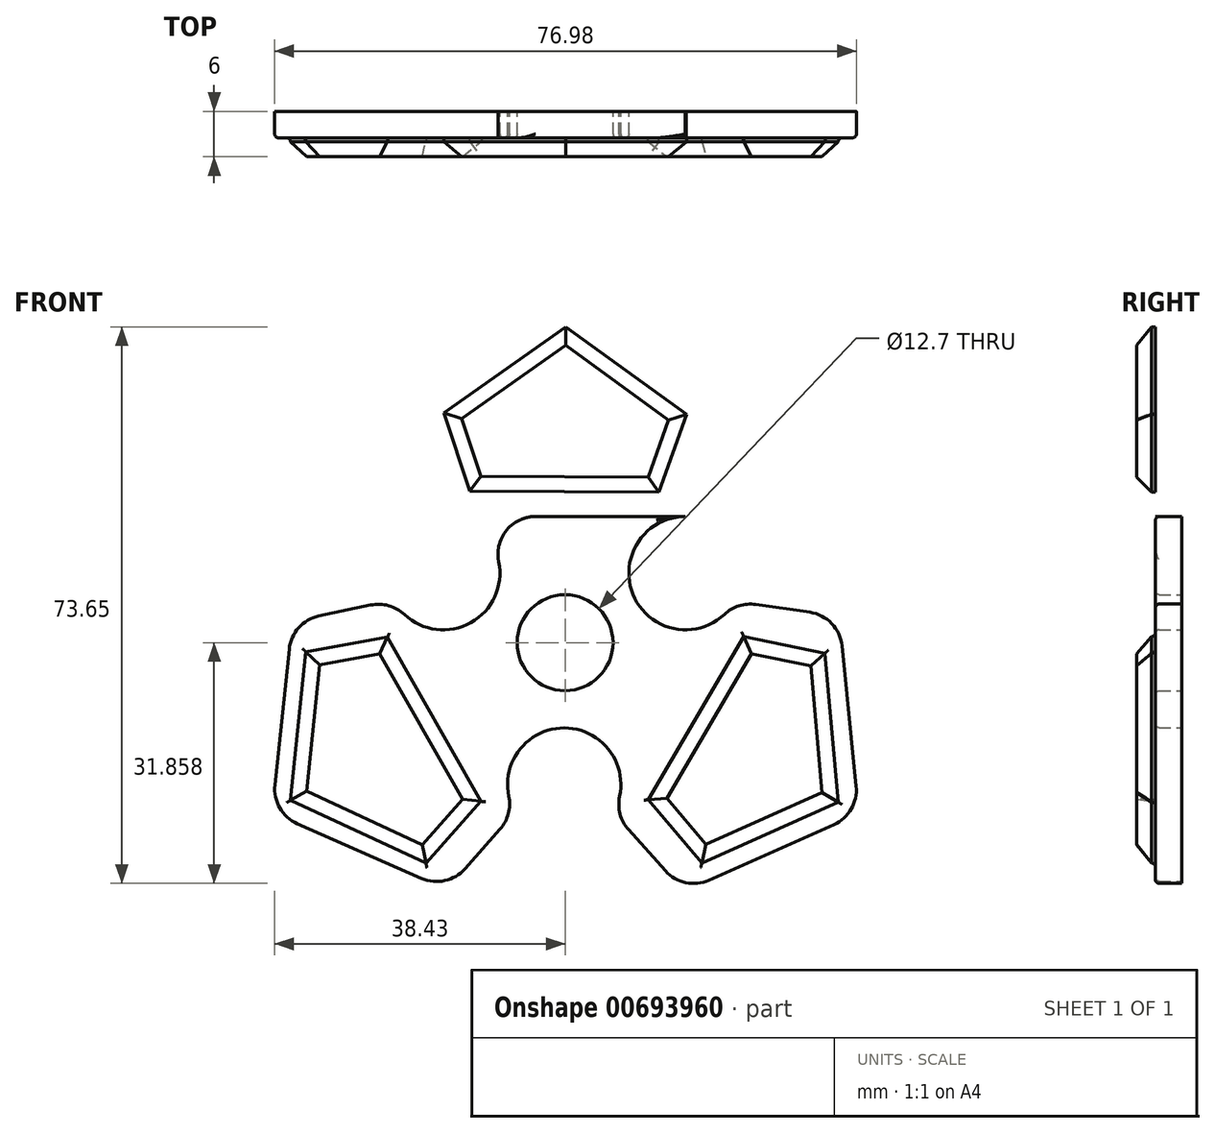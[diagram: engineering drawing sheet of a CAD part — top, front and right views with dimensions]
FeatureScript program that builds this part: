
annotation { "Feature Type Name" : "Feature", "Feature Type Description" : "" }
export const myFeature = defineFeature(function(context is Context, id is Id, definition is map)
    precondition{}
    {
        {
            var Q0;
            Q0=qCreatedBy(makeId("Front.planeOp"),FACE);
            var sketch = newSketch(context, id + "F0", { "sketchPlane" : qUnion([Q0])});
            skPoint(sketch, "E0.center", {"position": v(-0.03, -0.92) * mm});
            skLineSegment(sketch, "E1.0", {"start": v(15.99, 15.77) * mm, "end": v(-16.16, 15.77) * mm});
            skLineSegment(sketch, "E1.1", {"start": v(-16.16, 15.77) * mm, "end": v(-20.52, 29.1) * mm});
            skLineSegment(sketch, "E1.2", {"start": v(-20.52, 29.1) * mm, "end": v(0, 44.01) * mm});
            skLineSegment(sketch, "E1.3", {"start": v(0, 44.01) * mm, "end": v(20.51, 29.1) * mm});
            skLineSegment(sketch, "E1.4", {"start": v(20.51, 29.1) * mm, "end": v(15.99, 15.77) * mm});
            skPoint(sketch, "E1.0.midPoint", {"position": v(-0.09, 15.77) * mm});
            skLineSegment(sketch, "E2.1.0", {"start": v(22.42, 4.54) * mm, "end": v(36.23, 2.53) * mm});
            skLineSegment(sketch, "E2.1.2", {"start": v(36.23, 2.53) * mm, "end": v(38.86, -23.51) * mm});
            skLineSegment(sketch, "E2.1.3", {"start": v(6.36, -23.44) * mm, "end": v(22.42, 4.54) * mm});
            skLineSegment(sketch, "E2.1.4", {"start": v(15.7, -33.83) * mm, "end": v(6.36, -23.44) * mm});
            skLineSegment(sketch, "E2.1.5", {"start": v(38.86, -23.51) * mm, "end": v(15.7, -33.83) * mm});
            skLineSegment(sketch, "E2.2.0", {"start": v(-6.68, -23.39) * mm, "end": v(-15.67, -33.57) * mm});
            skLineSegment(sketch, "E2.2.2", {"start": v(-15.67, -33.57) * mm, "end": v(-38.81, -23.39) * mm});
            skLineSegment(sketch, "E2.2.3", {"start": v(-22.75, 4.69) * mm, "end": v(-6.68, -23.39) * mm});
            skLineSegment(sketch, "E2.2.4", {"start": v(-36.16, 1.84) * mm, "end": v(-22.75, 4.69) * mm});
            skLineSegment(sketch, "E2.2.5", {"start": v(-38.81, -23.39) * mm, "end": v(-36.16, 1.84) * mm});
            skPoint(sketch, "E2.center", {"position": v(0, -0.83) * mm});
            skArc(sketch, "E3", {"start": v(15.99, 15.77) * mm, "mid": v(9.4, 4.55) * mm, "end": v(22.42, 4.54) * mm});
            skArc(sketch, "E4", {"start": v(-22.75, 4.69) * mm, "mid": v(-9.71, 4.44) * mm, "end": v(-16.16, 15.77) * mm});
            skArc(sketch, "E5", {"start": v(6.36, -23.44) * mm, "mid": v(-0.11, -12.2) * mm, "end": v(-6.68, -23.39) * mm});
            skCircle(sketch, "E6", {"center": v(-0.03, -0.92) * mm, "radius": 6.35 * mm});
            skSolve(sketch);
        }
        {
            var Q0;
            Q0=makeQuery(id+"F0.imprint","IMPRINT",FACE,{"disambiguationData":[TD([[makeQuery(id+"F0.imprint","IMPRINT",EDGE,{"derivedFrom":sQuery(id+"F0.wireOp",EDGE,"E2.1.0")}),-1.0]])]});
            var Q1;
            {var subQ0=sQuery(id+"F0.wireOp",EDGE,"E1.0");Q1=makeQuery(id+"F0.imprint","IMPRINT",FACE,{"disambiguationData":[TD([[makeQuery(id+"F0.imprint","IMPRINT",EDGE,{"derivedFrom":subQ0}),-1.0]])]});}
            var Q2;
            {var subQ5=sQuery(id+"F0.wireOp",EDGE,"E1.0");Q2=makeQuery(id+"F0.imprint","IMPRINT",FACE,{"disambiguationData":[TD([[makeQuery(id+"F0.imprint","IMPRINT",EDGE,{"derivedFrom":subQ5}),1.0]])]});}
            var Q3;
            {var subQ2=sQuery(id+"F0.wireOp",EDGE,"E2.2.0");Q3=makeQuery(id+"F0.imprint","IMPRINT",FACE,{"disambiguationData":[TD([[makeQuery(id+"F0.imprint","IMPRINT",EDGE,{"derivedFrom":subQ2}),-1.0]])]});}
            extrude(context, id + "F1", {"entities" : qUnion([Q0, Q1, Q2, Q3]), "depth" : 3.5 * mm, "offsetDistance" : 25 * mm});
        }
        {
            var Q0;
            Q0=makeQuery(id+"F1.opExtrude","CAP_FACE",FACE,{"disambiguationData":[OSD([sQuery(id+"F0.wireOp",EDGE,"E1.1"),sQuery(id+"F0.wireOp",EDGE,"E1.2"),sQuery(id+"F0.wireOp",EDGE,"E1.3"),sQuery(id+"F0.wireOp",EDGE,"E1.4"),sQuery(id+"F0.wireOp",EDGE,"E2.1.0"),sQuery(id+"F0.wireOp",EDGE,"E2.1.2"),sQuery(id+"F0.wireOp",EDGE,"E2.1.4"),sQuery(id+"F0.wireOp",EDGE,"E2.1.5"),sQuery(id+"F0.wireOp",EDGE,"E2.2.0"),sQuery(id+"F0.wireOp",EDGE,"E2.2.2"),sQuery(id+"F0.wireOp",EDGE,"E2.2.4"),sQuery(id+"F0.wireOp",EDGE,"E2.2.5"),sQuery(id+"F0.wireOp",EDGE,"E3"),sQuery(id+"F0.wireOp",EDGE,"E4"),sQuery(id+"F0.wireOp",EDGE,"E5")])],"isStart":false});
            var sketch = newSketch(context, id + "F2", { "sketchPlane" : qUnion([Q0])});
            skLineSegment(sketch, "E7.0", {"start": v(12.36, 18.97) * mm, "end": v(-12.64, 19.1) * mm});
            skLineSegment(sketch, "E7.1", {"start": v(-12.64, 19.1) * mm, "end": v(-16.08, 29.5) * mm});
            skLineSegment(sketch, "E7.2", {"start": v(-16.08, 29.5) * mm, "end": v(0.08, 40.87) * mm});
            skLineSegment(sketch, "E7.3", {"start": v(0.08, 40.87) * mm, "end": v(16.07, 29.27) * mm});
            skLineSegment(sketch, "E7.4", {"start": v(16.07, 29.27) * mm, "end": v(12.36, 18.97) * mm});
            skLineSegment(sketch, "E8.1.0", {"start": v(-23.54, -0.2) * mm, "end": v(-11.15, -21.92) * mm});
            skLineSegment(sketch, "E8.1.1", {"start": v(-34.32, -2.14) * mm, "end": v(-23.54, -0.2) * mm});
            skLineSegment(sketch, "E8.1.2", {"start": v(-36.37, -21.8) * mm, "end": v(-34.32, -2.14) * mm});
            skLineSegment(sketch, "E8.1.3", {"start": v(-18.44, -30.1) * mm, "end": v(-36.37, -21.8) * mm});
            skLineSegment(sketch, "E8.1.4", {"start": v(-11.15, -21.92) * mm, "end": v(-18.44, -30.1) * mm});
            skLineSegment(sketch, "E8.2.0", {"start": v(11.01, -21.7) * mm, "end": v(23.62, -0.12) * mm});
            skLineSegment(sketch, "E8.2.1", {"start": v(18.08, -30.08) * mm, "end": v(11.01, -21.7) * mm});
            skLineSegment(sketch, "E8.2.2", {"start": v(36.12, -22.02) * mm, "end": v(18.08, -30.08) * mm});
            skLineSegment(sketch, "E8.2.3", {"start": v(34.34, -2.35) * mm, "end": v(36.12, -22.02) * mm});
            skLineSegment(sketch, "E8.2.4", {"start": v(23.62, -0.12) * mm, "end": v(34.34, -2.35) * mm});
            skPoint(sketch, "E8.center", {"position": v(-0.06, -0.98) * mm});
            skSolve(sketch);
        }
        {
            var Q0;
            Q0=makeQuery(id+"F2.imprint","IMPRINT",FACE,{"disambiguationData":[TD([[makeQuery(id+"F2.imprint","IMPRINT",EDGE,{"derivedFrom":sQuery(id+"F2.wireOp",EDGE,"E7.0")}),-1.0]])]});
            var Q1;
            Q1=makeQuery(id+"F2.imprint","IMPRINT",FACE,{"disambiguationData":[TD([[makeQuery(id+"F2.imprint","IMPRINT",EDGE,{"derivedFrom":sQuery(id+"F2.wireOp",EDGE,"E8.1.0")}),-1.0]])]});
            var Q2;
            Q2=makeQuery(id+"F2.imprint","IMPRINT",FACE,{"disambiguationData":[TD([[makeQuery(id+"F2.imprint","IMPRINT",EDGE,{"derivedFrom":sQuery(id+"F2.wireOp",EDGE,"E8.2.0")}),-1.0]])]});
            extrude(context, id + "F3", {"entities" : qUnion([Q0, Q1, Q2]), "operationType" : NewBodyOperationType.ADD, "depth" : 2.5 * mm, "offsetDistance" : 25 * mm});
        }
        {
            var Q0;
            Q0=makeQuery(id+"F3.opExtrude","CAP_FACE",FACE,{"disambiguationData":[OSD([sQuery(id+"F2.wireOp",EDGE,"E7.0"),sQuery(id+"F2.wireOp",EDGE,"E7.1"),sQuery(id+"F2.wireOp",EDGE,"E7.2"),sQuery(id+"F2.wireOp",EDGE,"E7.3"),sQuery(id+"F2.wireOp",EDGE,"E7.4")])],"isStart":false});
            var Q1;
            Q1=makeQuery(id+"F3.opExtrude","CAP_FACE",FACE,{"disambiguationData":[OSD([sQuery(id+"F2.wireOp",EDGE,"E8.2.0"),sQuery(id+"F2.wireOp",EDGE,"E8.2.1"),sQuery(id+"F2.wireOp",EDGE,"E8.2.2"),sQuery(id+"F2.wireOp",EDGE,"E8.2.3"),sQuery(id+"F2.wireOp",EDGE,"E8.2.4")])],"isStart":false});
            var Q2;
            Q2=makeQuery(id+"F3.opExtrude","CAP_FACE",FACE,{"disambiguationData":[OSD([sQuery(id+"F2.wireOp",EDGE,"E8.1.0"),sQuery(id+"F2.wireOp",EDGE,"E8.1.1"),sQuery(id+"F2.wireOp",EDGE,"E8.1.2"),sQuery(id+"F2.wireOp",EDGE,"E8.1.3"),sQuery(id+"F2.wireOp",EDGE,"E8.1.4")])],"isStart":false});
            chamfer(context, id + "F4", {"entities" : qUnion([Q0, Q1, Q2]), "width" : 2 * mm, "tangentPropagation" : true});
        }
        {
            var Q0;
            Q0=makeQuery(id+"F1.opExtrude","CAP_FACE",FACE,{"disambiguationData":[OSD([sQuery(id+"F0.wireOp",EDGE,"E1.1"),sQuery(id+"F0.wireOp",EDGE,"E1.2"),sQuery(id+"F0.wireOp",EDGE,"E1.3"),sQuery(id+"F0.wireOp",EDGE,"E1.4"),sQuery(id+"F0.wireOp",EDGE,"E2.1.0"),sQuery(id+"F0.wireOp",EDGE,"E2.1.2"),sQuery(id+"F0.wireOp",EDGE,"E2.1.4"),sQuery(id+"F0.wireOp",EDGE,"E2.1.5"),sQuery(id+"F0.wireOp",EDGE,"E2.2.0"),sQuery(id+"F0.wireOp",EDGE,"E2.2.2"),sQuery(id+"F0.wireOp",EDGE,"E2.2.4"),sQuery(id+"F0.wireOp",EDGE,"E2.2.5"),sQuery(id+"F0.wireOp",EDGE,"E3"),sQuery(id+"F0.wireOp",EDGE,"E4"),sQuery(id+"F0.wireOp",EDGE,"E5"),sQuery(id+"F0.wireOp",EDGE,"E6")])],"isStart":false});
            fillet(context, id + "F5", {"entities" : qUnion([Q0]), "radius" : 0.5 * mm, "tangentPropagation" : true, "allowEdgeOverflow" : false});
        }
        {
            var Q0;
            Q0=makeQuery(id+"F1.opExtrude","SWEPT_EDGE",EDGE,{"disambiguationData":[OSD([sQuery(id+"F0.wireOp",EDGE,"E1.0"),sQuery(id+"F0.wireOp",EDGE,"E1.1"),sQuery(id+"F0.wireOp",EDGE,"E4")])]});
            var Q1;
            Q1=makeQuery(id+"F1.opExtrude","SWEPT_EDGE",EDGE,{"disambiguationData":[OSD([sQuery(id+"F0.wireOp",EDGE,"E1.1"),sQuery(id+"F0.wireOp",EDGE,"E1.2")])]});
            var Q2;
            Q2=makeQuery(id+"F1.opExtrude","SWEPT_EDGE",EDGE,{"disambiguationData":[OSD([sQuery(id+"F0.wireOp",EDGE,"E1.2"),sQuery(id+"F0.wireOp",EDGE,"E1.3")])]});
            var Q3;
            Q3=makeQuery(id+"F1.opExtrude","SWEPT_EDGE",EDGE,{"disambiguationData":[OSD([sQuery(id+"F0.wireOp",EDGE,"E1.3"),sQuery(id+"F0.wireOp",EDGE,"E1.4")])]});
            var Q4;
            Q4=makeQuery(id+"F1.opExtrude","SWEPT_EDGE",EDGE,{"disambiguationData":[OSD([sQuery(id+"F0.wireOp",EDGE,"E1.4"),sQuery(id+"F0.wireOp",EDGE,"E3")])]});
            fillet(context, id + "F6", {"entities" : qUnion([Q0, Q1, Q2, Q3, Q4]), "radius" : 5 * mm, "tangentPropagation" : true, "allowEdgeOverflow" : false});
        }
        {
            var Q0;
            Q0=makeQuery(id+"F1.opExtrude","SWEPT_EDGE",EDGE,{"disambiguationData":[OSD([sQuery(id+"F0.wireOp",EDGE,"E2.1.4"),sQuery(id+"F0.wireOp",EDGE,"E2.1.5")])]});
            var Q1;
            Q1=makeQuery(id+"F1.opExtrude","SWEPT_EDGE",EDGE,{"disambiguationData":[OSD([sQuery(id+"F0.wireOp",EDGE,"E2.1.3"),sQuery(id+"F0.wireOp",EDGE,"E2.1.4"),sQuery(id+"F0.wireOp",EDGE,"E5")])]});
            var Q2;
            Q2=makeQuery(id+"F1.opExtrude","SWEPT_EDGE",EDGE,{"disambiguationData":[OSD([sQuery(id+"F0.wireOp",EDGE,"E2.1.2"),sQuery(id+"F0.wireOp",EDGE,"E2.1.5")])]});
            var Q3;
            Q3=makeQuery(id+"F1.opExtrude","SWEPT_EDGE",EDGE,{"disambiguationData":[OSD([sQuery(id+"F0.wireOp",EDGE,"E2.1.0"),sQuery(id+"F0.wireOp",EDGE,"E2.1.2")])]});
            var Q4;
            Q4=makeQuery(id+"F1.opExtrude","SWEPT_EDGE",EDGE,{"disambiguationData":[OSD([sQuery(id+"F0.wireOp",EDGE,"E2.1.0"),sQuery(id+"F0.wireOp",EDGE,"E2.1.3"),sQuery(id+"F0.wireOp",EDGE,"E3")])]});
            fillet(context, id + "F7", {"entities" : qUnion([Q0, Q1, Q2, Q3, Q4]), "radius" : 5 * mm, "tangentPropagation" : true, "allowEdgeOverflow" : false});
        }
        {
            var Q0;
            Q0=makeQuery(id+"F1.opExtrude","SWEPT_EDGE",EDGE,{"disambiguationData":[OSD([sQuery(id+"F0.wireOp",EDGE,"E2.2.0"),sQuery(id+"F0.wireOp",EDGE,"E2.2.2")])]});
            var Q1;
            Q1=makeQuery(id+"F1.opExtrude","SWEPT_EDGE",EDGE,{"disambiguationData":[OSD([sQuery(id+"F0.wireOp",EDGE,"E2.2.0"),sQuery(id+"F0.wireOp",EDGE,"E2.2.3"),sQuery(id+"F0.wireOp",EDGE,"E5")])]});
            var Q2;
            Q2=makeQuery(id+"F1.opExtrude","SWEPT_EDGE",EDGE,{"disambiguationData":[OSD([sQuery(id+"F0.wireOp",EDGE,"E2.2.2"),sQuery(id+"F0.wireOp",EDGE,"E2.2.5")])]});
            var Q3;
            Q3=makeQuery(id+"F1.opExtrude","SWEPT_EDGE",EDGE,{"disambiguationData":[OSD([sQuery(id+"F0.wireOp",EDGE,"E2.2.4"),sQuery(id+"F0.wireOp",EDGE,"E2.2.5")])]});
            var Q4;
            Q4=makeQuery(id+"F1.opExtrude","SWEPT_EDGE",EDGE,{"disambiguationData":[OSD([sQuery(id+"F0.wireOp",EDGE,"E2.2.3"),sQuery(id+"F0.wireOp",EDGE,"E2.2.4"),sQuery(id+"F0.wireOp",EDGE,"E4")])]});
            fillet(context, id + "F8", {"entities" : qUnion([Q0, Q1, Q2, Q3, Q4]), "radius" : 5 * mm, "tangentPropagation" : true, "allowEdgeOverflow" : false});
        }
    });
